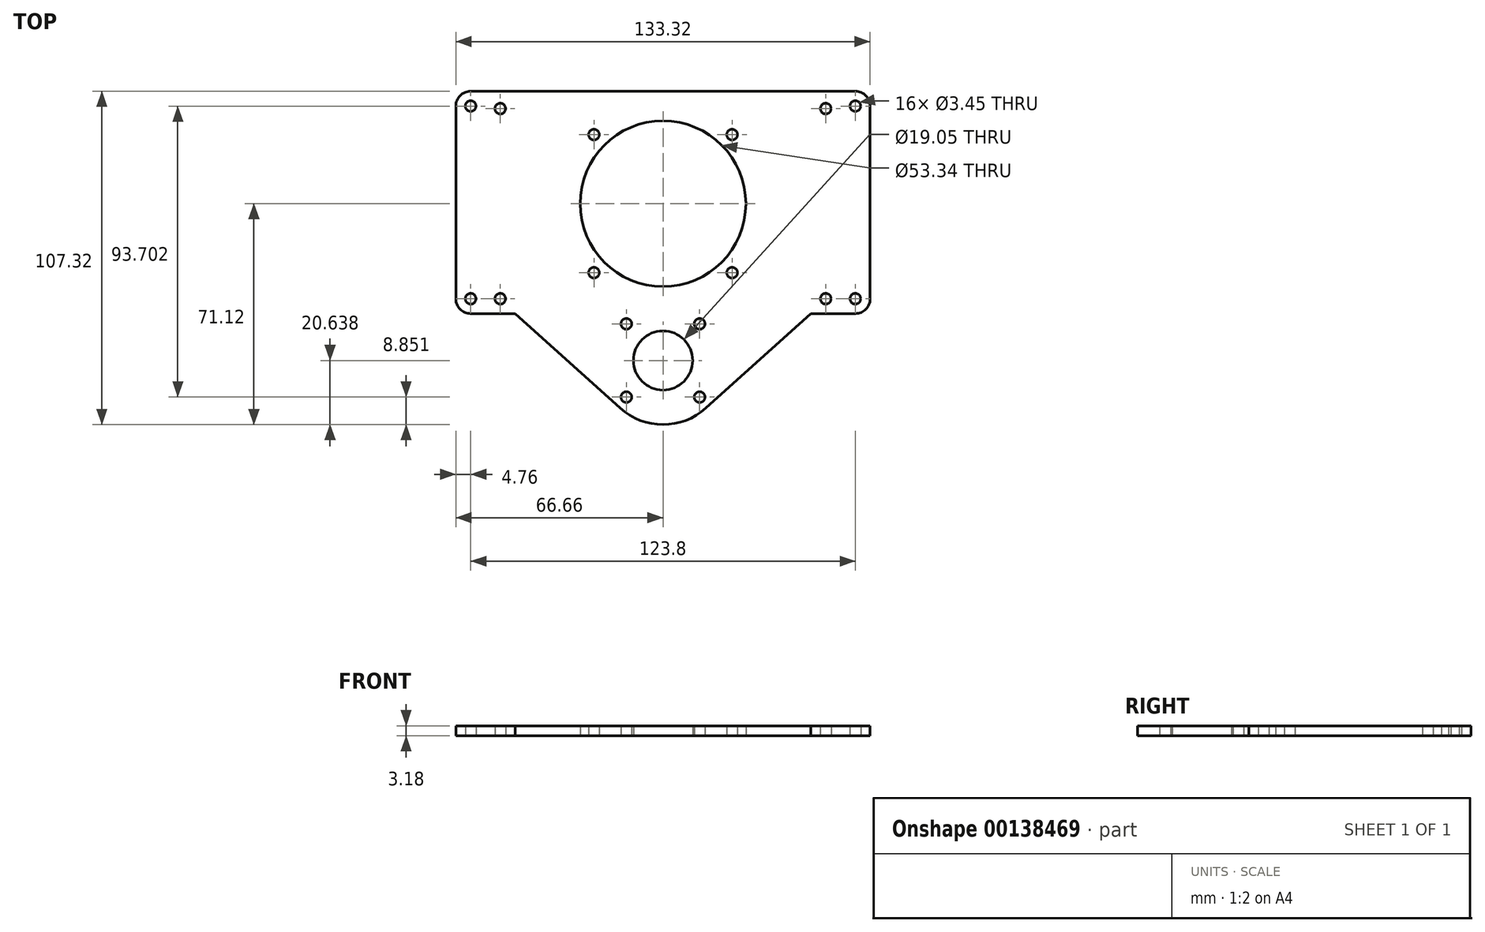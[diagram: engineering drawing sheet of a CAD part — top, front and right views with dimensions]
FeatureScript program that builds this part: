
annotation { "Feature Type Name" : "Feature", "Feature Type Description" : "" }
export const myFeature = defineFeature(function(context is Context, id is Id, definition is map)
    precondition{}
    {
        {
            var Q0;
            Q0=qCreatedBy(makeId("Top.planeOp"),FACE);
            var sketch = newSketch(context, id + "F0", { "sketchPlane" : qUnion([Q0])});
            skCircle(sketch, "E0", {"center": v(0, 0) * mm, "radius": 26.67 * mm});
            skLineSegment(sketch, "E1", {"start": v(-52.37, 0) * mm, "end": v(52.37, 0) * mm, "construction": true});
            skLineSegment(sketch, "E2", {"start": v(52.37, 30.6) * mm, "end": v(52.37, -30.6) * mm, "construction": true});
            skLineSegment(sketch, "E3", {"start": v(-52.37, 30.6) * mm, "end": v(-52.37, -30.6) * mm, "construction": true});
            skCircle(sketch, "E4", {"center": v(-52.37, 30.6) * mm, "radius": 1.73 * mm});
            skCircle(sketch, "E5", {"center": v(-52.37, -30.6) * mm, "radius": 1.73 * mm});
            skCircle(sketch, "E6", {"center": v(52.37, -30.6) * mm, "radius": 1.73 * mm});
            skCircle(sketch, "E7", {"center": v(52.37, 30.6) * mm, "radius": 1.73 * mm});
            skLineSegment(sketch, "E8.bottom", {"start": v(22.23, 22.23) * mm, "end": v(-22.23, 22.23) * mm, "construction": true});
            skLineSegment(sketch, "E8.top", {"start": v(22.23, -22.23) * mm, "end": v(-22.23, -22.23) * mm, "construction": true});
            skLineSegment(sketch, "E8.left", {"start": v(22.23, 22.23) * mm, "end": v(22.23, -22.23) * mm, "construction": true});
            skLineSegment(sketch, "E8.right", {"start": v(-22.23, 22.23) * mm, "end": v(-22.23, -22.23) * mm, "construction": true});
            skCircle(sketch, "E9", {"center": v(-22.23, 22.23) * mm, "radius": 4.76 * mm, "construction": true});
            skCircle(sketch, "E10", {"center": v(-22.23, 22.23) * mm, "radius": 1.73 * mm});
            skCircle(sketch, "E11", {"center": v(22.23, 22.23) * mm, "radius": 1.73 * mm});
            skCircle(sketch, "E12", {"center": v(22.23, -22.23) * mm, "radius": 1.73 * mm});
            skCircle(sketch, "E13", {"center": v(-22.23, -22.23) * mm, "radius": 1.73 * mm});
            skLineSegment(sketch, "E14.bottom", {"start": v(-66.66, 36.2) * mm, "end": v(66.66, 36.2) * mm});
            skLineSegment(sketch, "E14.left", {"start": v(-66.66, 36.2) * mm, "end": v(-66.66, -35.37) * mm});
            skLineSegment(sketch, "E14.right", {"start": v(66.66, 36.2) * mm, "end": v(66.66, -35.37) * mm});
            skLineSegment(sketch, "E15", {"start": v(11.79, -38.7) * mm, "end": v(-11.79, -62.27) * mm, "construction": true});
            skCircle(sketch, "E16", {"center": v(0, -50.48) * mm, "radius": 9.53 * mm});
            skLineSegment(sketch, "E17", {"start": v(-11.79, -38.7) * mm, "end": v(11.79, -62.27) * mm, "construction": true});
            skLineSegment(sketch, "E18", {"start": v(61.9, 31.43) * mm, "end": v(61.9, 36.2) * mm, "construction": true});
            skLineSegment(sketch, "E19", {"start": v(61.9, 31.43) * mm, "end": v(66.66, 31.43) * mm, "construction": true});
            skLineSegment(sketch, "E20", {"start": v(-61.9, 31.43) * mm, "end": v(-66.66, 31.43) * mm, "construction": true});
            skCircle(sketch, "E21", {"center": v(61.9, 31.43) * mm, "radius": 1.73 * mm});
            skCircle(sketch, "E22", {"center": v(-61.9, 31.43) * mm, "radius": 1.73 * mm});
            skCircle(sketch, "E23", {"center": v(11.79, -38.7) * mm, "radius": 1.73 * mm});
            skLineSegment(sketch, "E24", {"start": v(0, 0) * mm, "end": v(0, -50.48) * mm, "construction": true});
            skCircle(sketch, "E25", {"center": v(-11.79, -38.7) * mm, "radius": 1.73 * mm});
            skCircle(sketch, "E26", {"center": v(-11.79, -62.27) * mm, "radius": 1.73 * mm});
            skCircle(sketch, "E27", {"center": v(11.79, -62.27) * mm, "radius": 1.73 * mm});
            skCircle(sketch, "E28", {"center": v(0, 0) * mm, "radius": 36.2 * mm, "construction": true});
            skLineSegment(sketch, "E29", {"start": v(0, 0) * mm, "end": v(0, 36.2) * mm, "construction": true});
            skLineSegment(sketch, "E30", {"start": v(-52.37, -30.6) * mm, "end": v(-61.9, -30.6) * mm, "construction": true});
            skLineSegment(sketch, "E31", {"start": v(-61.9, -30.6) * mm, "end": v(-66.66, -30.6) * mm, "construction": true});
            skLineSegment(sketch, "E32", {"start": v(52.37, -30.6) * mm, "end": v(61.9, -30.6) * mm, "construction": true});
            skLineSegment(sketch, "E33", {"start": v(-61.9, -30.6) * mm, "end": v(-61.9, -35.37) * mm, "construction": true});
            skLineSegment(sketch, "E34", {"start": v(-66.66, -35.37) * mm, "end": v(-47.61, -35.37) * mm});
            skLineSegment(sketch, "E35", {"start": v(66.66, -35.37) * mm, "end": v(47.61, -35.37) * mm});
            skLineSegment(sketch, "E36", {"start": v(-47.61, -35.37) * mm, "end": v(-13.81, -65.82) * mm});
            skLineSegment(sketch, "E37", {"start": v(47.61, -35.37) * mm, "end": v(13.81, -65.82) * mm});
            skArc(sketch, "E38", {"start": v(-13.81, -65.82) * mm, "mid": v(0, -71.12) * mm, "end": v(13.81, -65.82) * mm});
            skCircle(sketch, "E39", {"center": v(11.79, -62.27) * mm, "radius": 3.97 * mm, "construction": true});
            skCircle(sketch, "E40", {"center": v(61.9, -30.6) * mm, "radius": 1.73 * mm});
            skCircle(sketch, "E41", {"center": v(-61.9, -30.6) * mm, "radius": 1.73 * mm});
            skSolve(sketch);
        }
        {
            var Q0;
            Q0 = qSketchRegion(id + "F0", true);
            extrude(context, id + "F1", {"entities" : qUnion([Q0]), "depth" : 3.17 * mm});
        }
        {
            var Q0;
            Q0=makeQuery(id+"F1.opExtrude","SWEPT_EDGE",EDGE,{"disambiguationData":[OSD([sQuery(id+"F0.wireOp",EDGE,"E14.bottom"),sQuery(id+"F0.wireOp",EDGE,"E14.left")])]});
            var Q1;
            Q1=makeQuery(id+"F1.opExtrude","SWEPT_EDGE",EDGE,{"disambiguationData":[OSD([sQuery(id+"F0.wireOp",EDGE,"E14.bottom"),sQuery(id+"F0.wireOp",EDGE,"E14.right")])]});
            var Q2;
            Q2=makeQuery(id+"F1.opExtrude","SWEPT_EDGE",EDGE,{"disambiguationData":[OSD([sQuery(id+"F0.wireOp",EDGE,"E14.right"),sQuery(id+"F0.wireOp",EDGE,"E35")])]});
            var Q3;
            Q3=makeQuery(id+"F1.opExtrude","SWEPT_EDGE",EDGE,{"disambiguationData":[OSD([sQuery(id+"F0.wireOp",EDGE,"E14.left"),sQuery(id+"F0.wireOp",EDGE,"E34")])]});
            fillet(context, id + "F2", {"entities" : qUnion([Q0, Q1, Q2, Q3]), "radius" : 4.76 * mm, "tangentPropagation" : true, "allowEdgeOverflow" : false});
        }
    });
